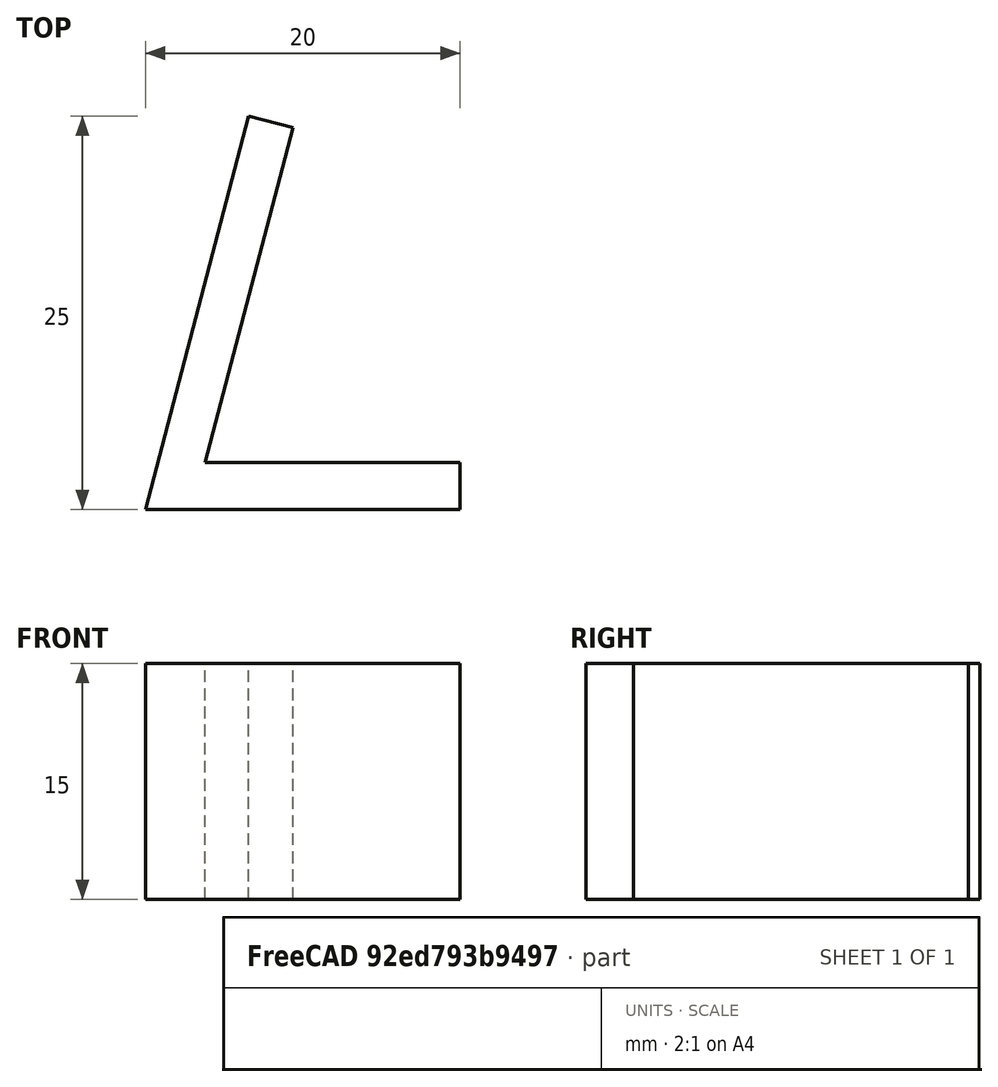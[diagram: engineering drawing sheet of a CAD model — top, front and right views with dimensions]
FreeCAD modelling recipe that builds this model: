
FCSTD DOCUMENT  (FreeCAD 2022.111R30764 (Git))
Label: cat odo water anti push tab
License: All rights reserved
LicenseURL: http://en.wikipedia.org/wiki/All_rights_reserved
objects: Sketcher::SketchObject×1, PartDesign::Pad×1, PartDesign::Body×1
note: 5 computed .brp shape members not serialized (recipe doc carries the construction recipe); baked Part::Feature solids carry a one-line shape summary decoded from their .brp

FEATURE [Sketcher::SketchObject] Sketch
  FullyConstrained = false
  MapMode = 5
  Support = -> [XY_Plane]
  TreeRank = 11
  sketch-geometry (7):
    g0: LineSegment StartX=20 StartY=0 StartZ=0 EndX=0 EndY=0 EndZ=0
    g1: LineSegment StartX=9.3696 StartY=24.2632 StartZ=0 EndX=3.78756 EndY=3 EndZ=0
    g2: LineSegment StartX=3.78756 StartY=3 StartZ=0 EndX=20 EndY=3 EndZ=0
    g3: LineSegment StartX=20 StartY=3 StartZ=0 EndX=20 EndY=0 EndZ=0
    g4: LineSegment StartX=6.56302 StartY=25 StartZ=0 EndX=9.3696 EndY=24.2632 EndZ=0
    g5: LineSegment StartX=6.56302 StartY=25 StartZ=0 EndX=0 EndY=0 EndZ=0
    g6: GeomPoint [constr] X=0.787562 Y=3 Z=0
  constraints (18):
    c: PointOnObject(g0,g-1)
    c: Coincident(g0,g-1)
    c: Coincident(g1,g2)
    c: Horizontal(g2)
    c: Coincident(g2,g3)
    c: Coincident(g3,g0)
    c: DistanceY(g3,g3) = 3
    c: DistanceY(g0,g4) = 25
    c: DistanceX(g0,g0) = 20
    c: Vertical(g3)
    c: Coincident(g4,g1)
    c: Perpendicular(g4,g1)
    c: Coincident(g5,g4)
    c: Coincident(g5,g0)
    c: Parallel(g1,g5)
    c: PointOnObject(g6,g5)
    c: Horizontal(g6,g1)
    c: DistanceX(g6,g1) = 3
FEATURE [PartDesign::Pad] Pad
  AddSubType = 0
  AlongSketchNormal = false
  CheckUpToFaceLimits = true
  ClaimChildren = false
  Direction = (0,0,1)
  Fit = 0
  FitJoin = 0
  InnerFit = 0
  InnerFitJoin = 0
  InnerTaperAngle = 0
  InnerTaperAngleRev = 0
  Length = 15
  Length2 = 100
  Linearize = true
  NewSolid = false
  Profile = -> Sketch
  Suppress = false
  TreeRank = 12
  Type = 0
  _ProfileBasedVersion = 1
FEATURE [PartDesign::Body] Body
  AutoGroupSolids = false
  ExportMode = 0
  Group = -> [Sketch,Pad]
  Origin = -> Origin
  Tip = -> Pad
  TreeRank = 10
  _ExportChildren = -> [Pad]
  _GroupVersion = 1
